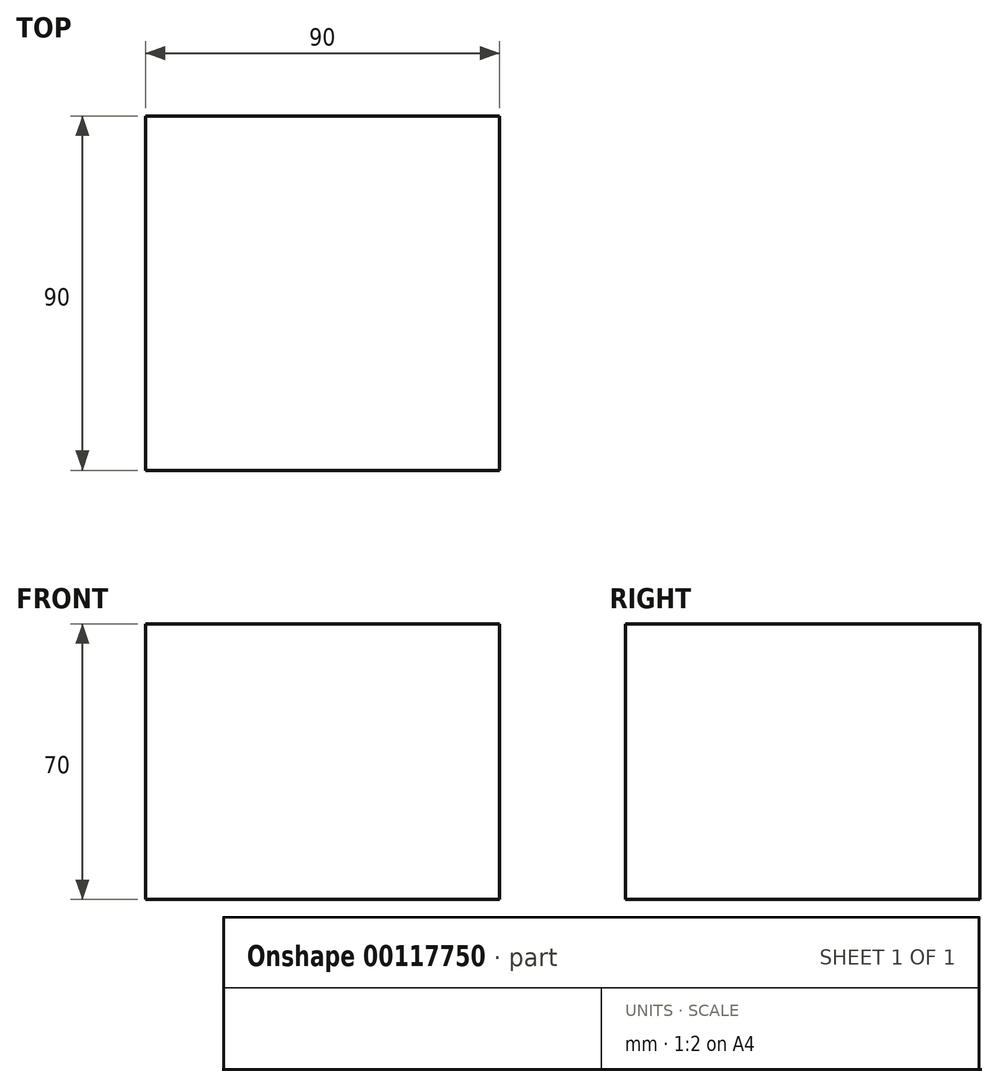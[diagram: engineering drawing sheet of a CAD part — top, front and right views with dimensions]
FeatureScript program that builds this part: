
annotation { "Feature Type Name" : "Feature", "Feature Type Description" : "" }
export const myFeature = defineFeature(function(context is Context, id is Id, definition is map)
    precondition{}
    {
        {
            var Q0;
            Q0=qCreatedBy(makeId("Front.planeOp"),FACE);
            var sketch = newSketch(context, id + "F0", { "sketchPlane" : qUnion([Q0])});
            skLineSegment(sketch, "E0.bottom", {"start": v(0, 0) * mm, "end": v(-90, 0) * mm});
            skLineSegment(sketch, "E0.top", {"start": v(0, 70) * mm, "end": v(-90, 70) * mm});
            skLineSegment(sketch, "E0.left", {"start": v(0, 0) * mm, "end": v(0, 70) * mm});
            skLineSegment(sketch, "E0.right", {"start": v(-90, 0) * mm, "end": v(-90, 70) * mm});
            skSolve(sketch);
        }
        {
            var Q0;
            Q0=makeQuery(id+"F0.imprint","IMPRINT",FACE,{"disambiguationData":[TD([[makeQuery(id+"F0.imprint","IMPRINT",EDGE,{"derivedFrom":sQuery(id+"F0.wireOp",EDGE,"E0.bottom")}),-1.0]])]});
            extrude(context, id + "F1", {"entities" : qUnion([Q0]), "depth" : 90 * mm});
        }
    });
